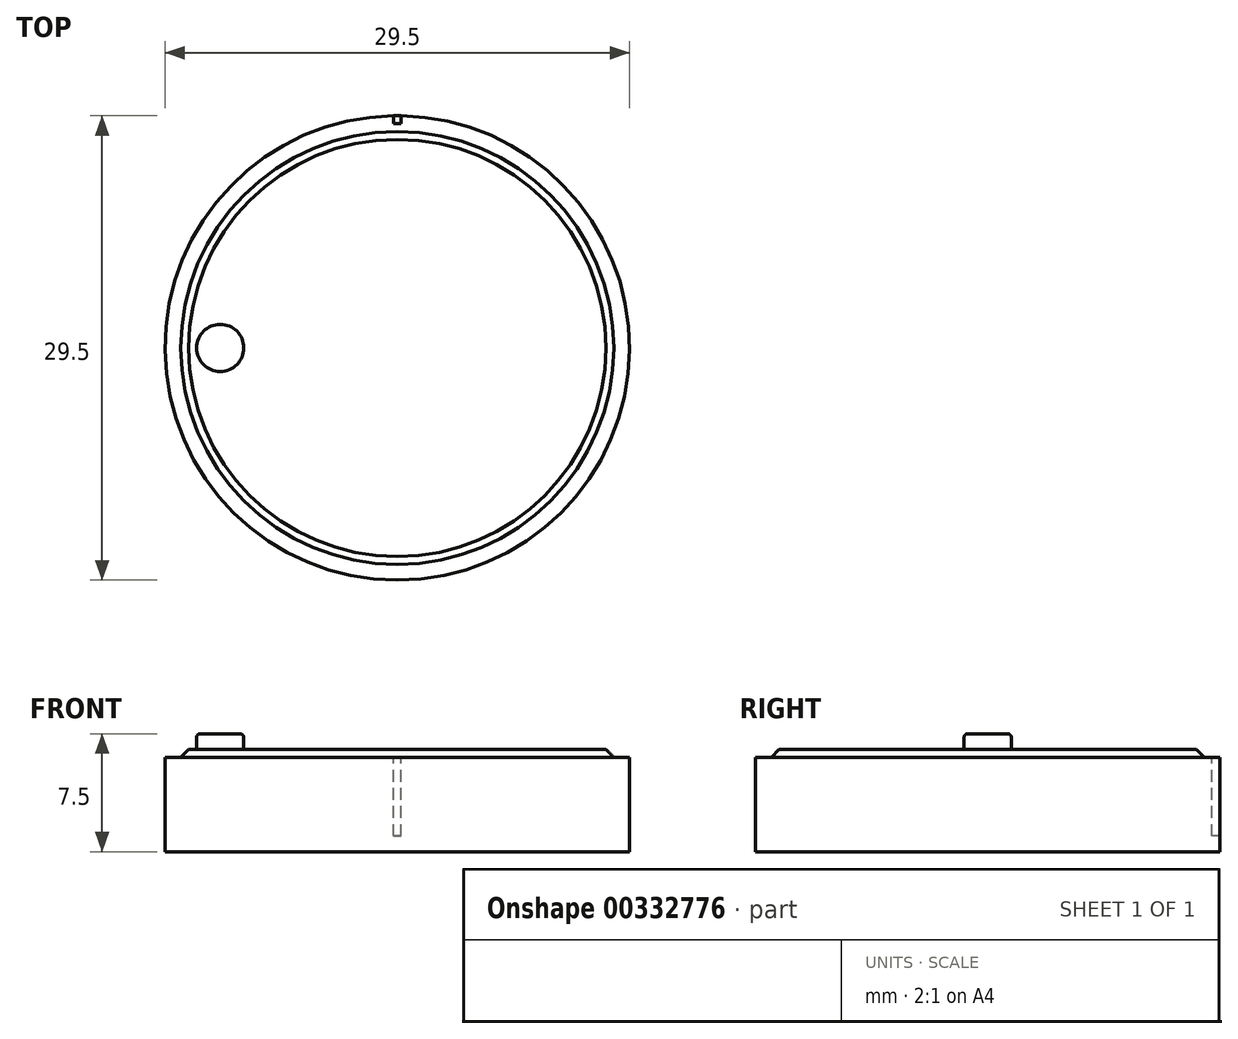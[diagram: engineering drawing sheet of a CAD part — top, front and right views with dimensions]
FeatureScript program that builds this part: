
annotation { "Feature Type Name" : "Feature", "Feature Type Description" : "" }
export const myFeature = defineFeature(function(context is Context, id is Id, definition is map)
    precondition{}
    {
        {
            var Q0;
            Q0=qCreatedBy(makeId("Top.planeOp"),FACE);
            var sketch = newSketch(context, id + "F0", { "sketchPlane" : qUnion([Q0])});
            skCircle(sketch, "E0", {"center": v(0, 0) * mm, "radius": 14.75 * mm});
            skSolve(sketch);
        }
        {
            var Q0;
            Q0=qSketchRegion(id+"F0",true);
            extrude(context, id + "F1", {"entities" : qUnion([Q0]), "depth" : 6 * mm});
        }
        {
            var Q0;
            Q0=makeQuery(id+"F1.opExtrude","CAP_FACE",FACE,{"disambiguationData":[OSD([sQuery(id+"F0.wireOp",EDGE,"E0")])],"isStart":false});
            var sketch = newSketch(context, id + "F2", { "sketchPlane" : qUnion([Q0])});
            skLineSegment(sketch, "E1.bottom", {"start": v(-0.25, 15.25) * mm, "end": v(0.25, 15.25) * mm});
            skLineSegment(sketch, "E1.top", {"start": v(-0.25, 14.25) * mm, "end": v(0.25, 14.25) * mm});
            skLineSegment(sketch, "E1.left", {"start": v(-0.25, 15.25) * mm, "end": v(-0.25, 14.25) * mm});
            skLineSegment(sketch, "E1.right", {"start": v(0.25, 15.25) * mm, "end": v(0.25, 14.25) * mm});
            skPoint(sketch, "E1.middle", {"position": v(0, 14.75) * mm});
            skSolve(sketch);
        }
        {
            var Q0;
            {var subQ0=sQuery(id+"F2.wireOp",EDGE,"E1.top");Q0=makeQuery(id+"F2.imprint","IMPRINT",FACE,{"disambiguationData":[TD([[makeQuery(id+"F2.imprint","IMPRINT",EDGE,{"derivedFrom":subQ0}),1.0]])]});}
            extrude(context, id + "F3", {"entities" : qUnion([Q0]), "operationType" : NewBodyOperationType.REMOVE, "oppositeDirection" : true, "depth" : 5 * mm});
        }
        {
            var Q0;
            Q0=makeQuery(id+"F1.opExtrude","CAP_FACE",FACE,{"disambiguationData":[OSD([sQuery(id+"F0.wireOp",EDGE,"E0")])],"isStart":false});
            var sketch = newSketch(context, id + "F4", { "sketchPlane" : qUnion([Q0])});
            skCircle(sketch, "E2", {"center": v(0, 0) * mm, "radius": 13.75 * mm});
            skSolve(sketch);
        }
        {
            var Q0;
            Q0=qSketchRegion(id+"F4",true);
            extrude(context, id + "F5", {"entities" : qUnion([Q0]), "operationType" : NewBodyOperationType.ADD, "depth" : 0.5 * mm});
        }
        {
            var Q0;
            Q0=makeQuery(id+"F5.opExtrude","CAP_FACE",FACE,{"disambiguationData":[OSD([sQuery(id+"F4.wireOp",EDGE,"E2")])],"isStart":false});
            var sketch = newSketch(context, id + "F6", { "sketchPlane" : qUnion([Q0])});
            skLineSegment(sketch, "E3", {"start": v(-13.75, 0) * mm, "end": v(-11.25, 0) * mm});
            skCircle(sketch, "E4", {"center": v(-11.25, 0) * mm, "radius": 1.5 * mm});
            skSolve(sketch);
        }
        {
            var Q0;
            Q0=qSketchRegion(id+"F6",true);
            extrude(context, id + "F7", {"entities" : qUnion([Q0]), "operationType" : NewBodyOperationType.ADD, "depth" : 1 * mm});
        }
        {
            var Q0;
            Q0=makeQuery(id+"FI4fiMxGAmJ1jl2_1.7.F7.opExtrude","CAP_EDGE",EDGE,{"disambiguationData":[OSD([sQuery(id+"F6.wireOp",EDGE,"E4")])],"isStart":false});
            var Q1;
            Q1=makeQuery(id+"FI4fiMxGAmJ1jl2_1.6.F7.opExtrude","CAP_EDGE",EDGE,{"disambiguationData":[OSD([sQuery(id+"F6.wireOp",EDGE,"E4")])],"isStart":false});
            var Q2;
            Q2=makeQuery(id+"FI4fiMxGAmJ1jl2_1.5.F7.opExtrude","CAP_EDGE",EDGE,{"disambiguationData":[OSD([sQuery(id+"F6.wireOp",EDGE,"E4")])],"isStart":false});
            var Q3;
            Q3=makeQuery(id+"FI4fiMxGAmJ1jl2_1.4.F7.opExtrude","CAP_EDGE",EDGE,{"disambiguationData":[OSD([sQuery(id+"F6.wireOp",EDGE,"E4")])],"isStart":false});
            var Q4;
            Q4=makeQuery(id+"FI4fiMxGAmJ1jl2_1.3.F7.opExtrude","CAP_EDGE",EDGE,{"disambiguationData":[OSD([sQuery(id+"F6.wireOp",EDGE,"E4")])],"isStart":false});
            var Q5;
            Q5=makeQuery(id+"FI4fiMxGAmJ1jl2_1.2.F7.opExtrude","CAP_EDGE",EDGE,{"disambiguationData":[OSD([sQuery(id+"F6.wireOp",EDGE,"E4")])],"isStart":false});
            var Q6;
            Q6=makeQuery(id+"FI4fiMxGAmJ1jl2_1.1.F7.opExtrude","CAP_EDGE",EDGE,{"disambiguationData":[OSD([sQuery(id+"F6.wireOp",EDGE,"E4")])],"isStart":false});
            var Q7;
            Q7=makeQuery(id+"F7.opExtrude","CAP_EDGE",EDGE,{"disambiguationData":[OSD([sQuery(id+"F6.wireOp",EDGE,"E4")])],"isStart":false});
            var Q8;
            Q8=makeQuery(id+"FI4fiMxGAmJ1jl2_1.8.F7.opExtrude","CAP_EDGE",EDGE,{"disambiguationData":[OSD([sQuery(id+"F6.wireOp",EDGE,"E4")])],"isStart":false});
            fillet(context, id + "F8", {"entities" : qUnion([Q0, Q1, Q2, Q3, Q4, Q5, Q6, Q7, Q8]), "radius" : 0.25 * mm, "tangentPropagation" : true, "allowEdgeOverflow" : false});
        }
        {
            var Q0;
            Q0=makeQuery(id+"F5.opExtrude","CAP_EDGE",EDGE,{"disambiguationData":[OSD([sQuery(id+"F4.wireOp",EDGE,"E2")])],"isStart":false});
            chamfer(context, id + "F9", {"entities" : qUnion([Q0]), "width" : 0.5 * mm, "tangentPropagation" : true});
        }
    });
